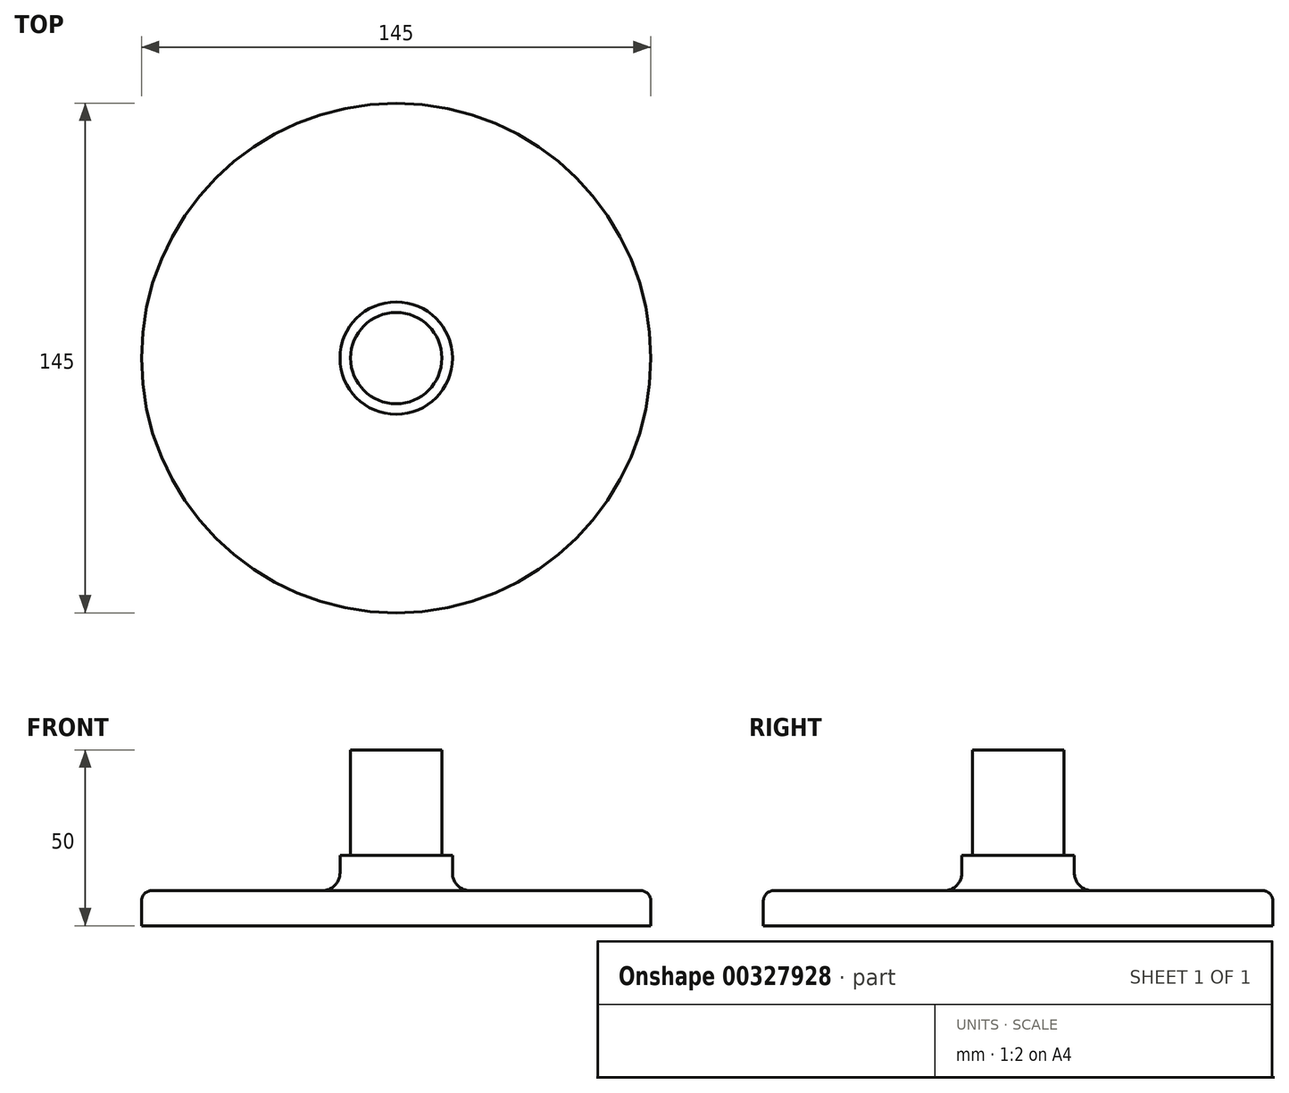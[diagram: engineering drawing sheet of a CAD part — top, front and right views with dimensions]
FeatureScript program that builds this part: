
annotation { "Feature Type Name" : "Feature", "Feature Type Description" : "" }
export const myFeature = defineFeature(function(context is Context, id is Id, definition is map)
    precondition{}
    {
        {
            var Q0;
            Q0=qCreatedBy(makeId("Top.planeOp"),FACE);
            var sketch = newSketch(context, id + "F0", { "sketchPlane" : qUnion([Q0])});
            skCircle(sketch, "E0", {"center": v(0, 0) * mm, "radius": 72.5 * mm});
            skSolve(sketch);
        }
        {
            var Q0;
            Q0 = qSketchRegion(id + "F0", true);
            extrude(context, id + "F1", {"entities" : qUnion([Q0]), "depth" : 10 * mm});
        }
        {
            var Q0;
            Q0=makeQuery(id+"F1.opExtrude","CAP_FACE",FACE,{"disambiguationData":[OSD([sQuery(id+"F0.wireOp",EDGE,"E0")])],"isStart":false});
            var sketch = newSketch(context, id + "F2", { "sketchPlane" : qUnion([Q0])});
            skCircle(sketch, "E1", {"center": v(0, 0) * mm, "radius": 16 * mm});
            skSolve(sketch);
        }
        {
            var Q0;
            Q0 = qSketchRegion(id + "F2", true);
            extrude(context, id + "F3", {"entities" : qUnion([Q0]), "operationType" : NewBodyOperationType.ADD, "depth" : 10 * mm});
        }
        {
            var Q0;
            Q0=makeQuery(id+"F3.opExtrude","CAP_FACE",FACE,{"disambiguationData":[OSD([sQuery(id+"F2.wireOp",EDGE,"E1")])],"isStart":false});
            var sketch = newSketch(context, id + "F4", { "sketchPlane" : qUnion([Q0])});
            skCircle(sketch, "E2", {"center": v(0, 0) * mm, "radius": 13 * mm});
            skSolve(sketch);
        }
        {
            var Q0;
            Q0 = qSketchRegion(id + "F4", true);
            extrude(context, id + "F5", {"entities" : qUnion([Q0]), "operationType" : NewBodyOperationType.ADD, "depth" : 30 * mm});
        }
        {
            var Q0;
            Q0=makeQuery(id+"F1.opExtrude","CAP_EDGE",EDGE,{"disambiguationData":[OSD([sQuery(id+"F0.wireOp",EDGE,"E0")])],"isStart":false});
            fillet(context, id + "F6", {"entities" : qUnion([Q0]), "radius" : 3 * mm, "tangentPropagation" : true, "allowEdgeOverflow" : false});
        }
        {
            var Q0;
            {var subQ0=sQuery(id+"F0.wireOp",EDGE,"E0");Q0=makeQuery(id+"F6.opFillet","BLEND_EDGE",EDGE,{"blendedFrom":[makeQuery(id+"F1.opExtrude","CAP_EDGE",EDGE,{"disambiguationData":[OSD([subQ0])],"isStart":false}),makeQuery(id+"F1.opExtrude","SWEPT_FACE",FACE,{"disambiguationData":[OSD([subQ0])]})],"blendedInto":[makeQuery(id+"F1.opExtrude","SWEPT_FACE",FACE,{"disambiguationData":[OSD([subQ0])]})]});}
            var Q1;
            Q1=makeQuery(id+"F1.opExtrude","CAP_FACE",FACE,{"disambiguationData":[OSD([sQuery(id+"F0.wireOp",EDGE,"E0")])],"isStart":false});
            fillet(context, id + "F7", {"entities" : qUnion([Q0, Q1]), "radius" : 5 * mm, "tangentPropagation" : true, "allowEdgeOverflow" : false});
        }
    });
